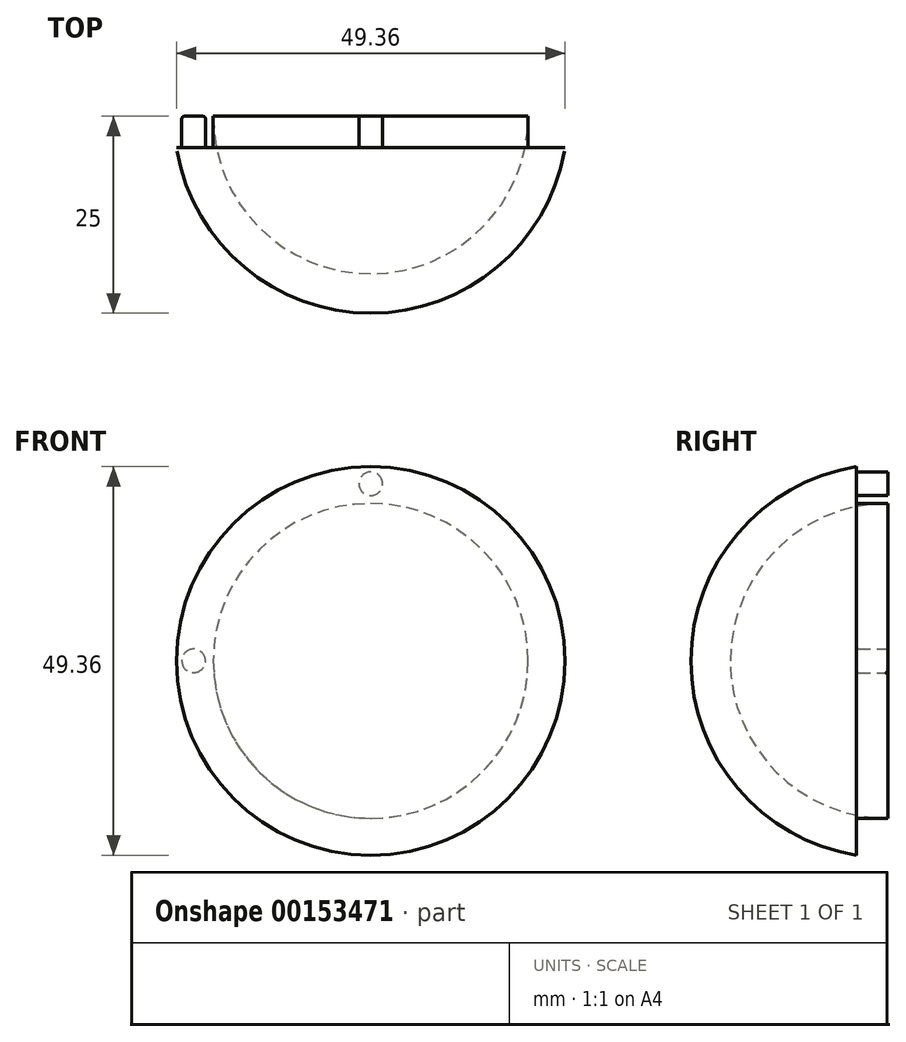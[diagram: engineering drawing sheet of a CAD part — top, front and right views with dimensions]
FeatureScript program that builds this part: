
annotation { "Feature Type Name" : "Feature", "Feature Type Description" : "" }
export const myFeature = defineFeature(function(context is Context, id is Id, definition is map)
    precondition{}
    {
        {
            var Q0;
            Q0=qCreatedBy(makeId("Front.planeOp"),FACE);
            var sketch = newSketch(context, id + "F0", { "sketchPlane" : qUnion([Q0])});
            skArc(sketch, "E0", {"start": v(-25, 0) * mm, "mid": v(0, -25) * mm, "end": v(25, 0) * mm});
            skArc(sketch, "E1", {"start": v(-20, 0) * mm, "mid": v(0, -20) * mm, "end": v(20, 0) * mm});
            skLineSegment(sketch, "E2", {"start": v(25, 0) * mm, "end": v(20, 0) * mm});
            skLineSegment(sketch, "E3", {"start": v(-20, 0) * mm, "end": v(-25, 0) * mm});
            skSolve(sketch);
        }
        {
            var Q0;
            Q0=qCreatedBy(makeId("Right.planeOp"),FACE);
            var sketch = newSketch(context, id + "F1", { "sketchPlane" : qUnion([Q0])});
            skLineSegment(sketch, "E4", {"start": v(0, 56.62) * mm, "end": v(0, -56.38) * mm, "construction": true});
            skSolve(sketch);
        }
        {
            var Q0;
            Q0=qCreatedBy(makeId("Front.planeOp"),FACE);
            var sketch = newSketch(context, id + "F2", { "sketchPlane" : qUnion([Q0])});
            skLineSegment(sketch, "E5", {"start": v(-74.79, 0) * mm, "end": v(75.26, 0) * mm, "construction": true});
            skSolve(sketch);
        }
        {
            var Q0;
            Q0=makeQuery(id+"F0.imprint","IMPRINT",FACE,{"disambiguationData":[TD([[makeQuery(id+"F0.imprint","IMPRINT",EDGE,{"derivedFrom":sQuery(id+"F0.wireOp",EDGE,"E0")}),1.0]])]});
            var Q1;
            Q1=sQuery(id+"F2.wireOp",EDGE,"E5");
            revolve(context, id + "F3", {"entities" : qUnion([Q0]), "axis" : qUnion([Q1]), "revolveType" : RevolveType.FULL});
        }
        {
            var Q0;
            Q0=qCreatedBy(makeId("Front.planeOp"),FACE);
            var sketch = newSketch(context, id + "F4", { "sketchPlane" : qUnion([Q0])});
            skLineSegment(sketch, "E6.bottom", {"start": v(-30, 30) * mm, "end": v(30, 30) * mm});
            skLineSegment(sketch, "E6.top", {"start": v(-30, -30) * mm, "end": v(30, -30) * mm});
            skLineSegment(sketch, "E6.left", {"start": v(-30, 30) * mm, "end": v(-30, -30) * mm});
            skLineSegment(sketch, "E6.right", {"start": v(30, 30) * mm, "end": v(30, -30) * mm});
            skSolve(sketch);
        }
        {
            var Q0;
            Q0 = qSketchRegion(id + "F4", true);
            extrude(context, id + "F5", {"entities" : qUnion([Q0]), "operationType" : NewBodyOperationType.REMOVE, "oppositeDirection" : true, "depth" : 30 * mm});
        }
        {
            var Q0;
            Q0=makeQuery(id+"F5.boolean.opBoolean","COPY",FACE,{"derivedFrom":makeQuery(id+"F5.opExtrude","CAP_FACE",FACE,{"disambiguationData":[OSD([sQuery(id+"F4.wireOp",EDGE,"E6.bottom"),sQuery(id+"F4.wireOp",EDGE,"E6.top"),sQuery(id+"F4.wireOp",EDGE,"E6.left"),sQuery(id+"F4.wireOp",EDGE,"E6.right")])],"isStart":true})});
            var sketch = newSketch(context, id + "F6", { "sketchPlane" : qUnion([Q0])});
            skCircle(sketch, "E7", {"center": v(0, 0) * mm, "radius": 22.5 * mm, "construction": true});
            skCircle(sketch, "E8", {"center": v(0, -22.5) * mm, "radius": 1.5 * mm});
            skCircle(sketch, "E9.MirrorC", {"center": v(0, 22.5) * mm, "radius": 1.5 * mm});
            skCircle(sketch, "E10", {"center": v(-22.5, 0) * mm, "radius": 1.5 * mm});
            skCircle(sketch, "E11.MirrorC", {"center": v(22.5, 0) * mm, "radius": 1.5 * mm});
            skSolve(sketch);
        }
        {
            var Q0;
            Q0=makeQuery(id+"F6.imprint","IMPRINT",FACE,{"disambiguationData":[TD([[makeQuery(id+"F6.imprint","IMPRINT",EDGE,{"derivedFrom":sQuery(id+"F6.wireOp",EDGE,"E10")}),1.0]])]});
            var Q1;
            Q1=makeQuery(id+"F6.imprint","IMPRINT",FACE,{"disambiguationData":[TD([[makeQuery(id+"F6.imprint","IMPRINT",EDGE,{"derivedFrom":sQuery(id+"F6.wireOp",EDGE,"E8")}),1.0]])]});
            var Q2;
            Q2=makeQuery(id+"F6.imprint","IMPRINT",FACE,{"disambiguationData":[TD([[makeQuery(id+"F6.imprint","IMPRINT",EDGE,{"derivedFrom":sQuery(id+"F6.wireOp",EDGE,"E9.MirrorC")}),-1.0]])]});
            var Q3;
            Q3=makeQuery(id+"F6.imprint","IMPRINT",FACE,{"disambiguationData":[TD([[makeQuery(id+"F6.imprint","IMPRINT",EDGE,{"derivedFrom":sQuery(id+"F6.wireOp",EDGE,"E11.MirrorC")}),-1.0]])]});
            extrude(context, id + "F7", {"entities" : qUnion([Q0, Q1, Q2, Q3]), "operationType" : NewBodyOperationType.REMOVE, "oppositeDirection" : true, "depth" : 4 * mm});
        }
        {
            var Q0;
            Q0=makeQuery(id+"F7.boolean.opBoolean","COPY",EDGE,{"derivedFrom":makeQuery(id+"F7.opExtrude","CAP_EDGE",EDGE,{"disambiguationData":[OSD([sQuery(id+"F6.wireOp",EDGE,"E11.MirrorC")])],"isStart":true})});
            var Q1;
            Q1=makeQuery(id+"F7.boolean.opBoolean","COPY",EDGE,{"derivedFrom":makeQuery(id+"F7.opExtrude","CAP_EDGE",EDGE,{"disambiguationData":[OSD([sQuery(id+"F6.wireOp",EDGE,"E9.MirrorC")])],"isStart":true})});
            var Q2;
            Q2=makeQuery(id+"F7.boolean.opBoolean","COPY",EDGE,{"derivedFrom":makeQuery(id+"F7.opExtrude","CAP_EDGE",EDGE,{"disambiguationData":[OSD([sQuery(id+"F6.wireOp",EDGE,"E8")])],"isStart":true})});
            var Q3;
            Q3=makeQuery(id+"F7.boolean.opBoolean","COPY",EDGE,{"derivedFrom":makeQuery(id+"F7.opExtrude","CAP_EDGE",EDGE,{"disambiguationData":[OSD([sQuery(id+"F6.wireOp",EDGE,"E10")])],"isStart":true})});
            fillet(context, id + "F8", {"entities" : qUnion([Q0, Q1, Q2, Q3]), "radius" : 0.3 * mm, "tangentPropagation" : true, "allowEdgeOverflow" : false});
        }
        {
            var Q0;
            Q0=makeQuery(id+"F7.boolean.opBoolean","COPY",EDGE,{"derivedFrom":makeQuery(id+"F7.opExtrude","CAP_EDGE",EDGE,{"disambiguationData":[OSD([sQuery(id+"F6.wireOp",EDGE,"E10")])],"isStart":false})});
            var Q1;
            Q1=makeQuery(id+"F7.boolean.opBoolean","COPY",EDGE,{"derivedFrom":makeQuery(id+"F7.opExtrude","CAP_EDGE",EDGE,{"disambiguationData":[OSD([sQuery(id+"F6.wireOp",EDGE,"E11.MirrorC")])],"isStart":false})});
            var Q2;
            Q2=makeQuery(id+"F7.boolean.opBoolean","COPY",EDGE,{"derivedFrom":makeQuery(id+"F7.opExtrude","CAP_EDGE",EDGE,{"disambiguationData":[OSD([sQuery(id+"F6.wireOp",EDGE,"E8")])],"isStart":false})});
            var Q3;
            Q3=makeQuery(id+"F7.boolean.opBoolean","COPY",EDGE,{"derivedFrom":makeQuery(id+"F7.opExtrude","CAP_EDGE",EDGE,{"disambiguationData":[OSD([sQuery(id+"F6.wireOp",EDGE,"E9.MirrorC")])],"isStart":false})});
            fillet(context, id + "F9", {"entities" : qUnion([Q0, Q1, Q2, Q3]), "radius" : 0.3 * mm, "tangentPropagation" : true, "allowEdgeOverflow" : false});
        }
    });
